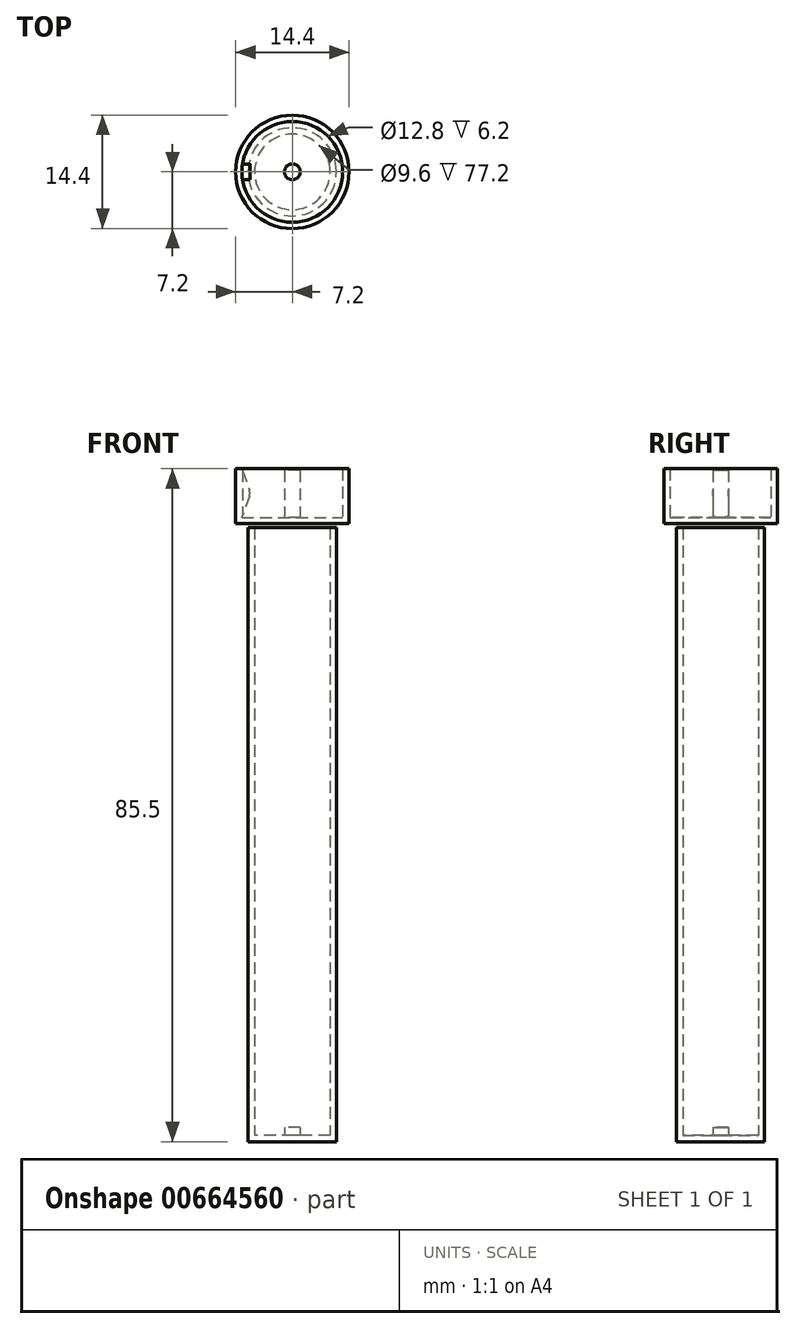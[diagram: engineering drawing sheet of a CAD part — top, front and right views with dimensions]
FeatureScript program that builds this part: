
annotation { "Feature Type Name" : "Feature", "Feature Type Description" : "" }
export const myFeature = defineFeature(function(context is Context, id is Id, definition is map)
    precondition{}
    {
        {
            var Q0;
            Q0=qCreatedBy(makeId("Top.planeOp"),FACE);
            var sketch = newSketch(context, id + "F0", { "sketchPlane" : qUnion([Q0])});
            skCircle(sketch, "E0", {"center": v(0, 0) * mm, "radius": 5.6 * mm});
            skSolve(sketch);
        }
        {
            var Q0;
            Q0=makeQuery(id+"F0.imprint","IMPRINT",FACE,{"disambiguationData":[TD([[makeQuery(id+"F0.imprint","IMPRINT",EDGE,{"derivedFrom":sQuery(id+"F0.wireOp",EDGE,"E0")}),1.0]])]});
            extrude(context, id + "F1", {"entities" : qUnion([Q0]), "depth" : 78 * mm, "offsetDistance" : 25 * mm});
        }
        {
            var Q0;
            Q0=makeQuery(id+"F1.opExtrude","CAP_FACE",FACE,{"disambiguationData":[OSD([sQuery(id+"F0.wireOp",EDGE,"E0")])],"isStart":false});
            shell(context, id + "F2", {"entities" : qUnion([Q0]), "thickness" : 0.8 * mm});
        }
        {
            var Q0;
            {var subQ0=sQuery(id+"F0.wireOp",EDGE,"E0");Q0=makeQuery(id+"F2.opShell","OFFSET_FACE",FACE,{"disambiguationData":[OSD([subQ0]),TDD([makeQuery(id+"F1.opExtrude","CAP_FACE",FACE,{"disambiguationData":[OSD([subQ0])],"isStart":true})])]});}
            var sketch = newSketch(context, id + "F3", { "sketchPlane" : qUnion([Q0])});
            skCircle(sketch, "E1", {"center": v(0, 0) * mm, "radius": 1 * mm});
            skSolve(sketch);
        }
        {
            var Q0;
            Q0 = qSketchRegion(id + "F3", true);
            extrude(context, id + "F4", {"entities" : qUnion([Q0]), "operationType" : NewBodyOperationType.ADD, "depth" : 1 * mm, "offsetDistance" : 25 * mm});
        }
        {
            var Q0;
            Q0=makeQuery(id+"F1.opExtrude","CAP_FACE",FACE,{"disambiguationData":[OSD([sQuery(id+"F0.wireOp",EDGE,"E0")])],"isStart":false});
            cPlane(context, id + "F5", {"entities" : qUnion([Q0]), "cplaneType" : CPlaneType.OFFSET, "offset" : 0.5 * mm, "width" : 150 * mm, "height" : 150 * mm});
        }
        {
            var Q0;
            Q0=qCreatedBy(id+"F5.planeOp",FACE);
            var sketch = newSketch(context, id + "F6", { "sketchPlane" : qUnion([Q0])});
            skCircle(sketch, "E2", {"center": v(0, 0) * mm, "radius": 7.2 * mm});
            skSolve(sketch);
        }
        {
            var Q0;
            Q0=makeQuery(id+"F6.imprint","IMPRINT",FACE,{"disambiguationData":[TD([[makeQuery(id+"F6.imprint","IMPRINT",EDGE,{"derivedFrom":sQuery(id+"F6.wireOp",EDGE,"E2")}),1.0]])]});
            extrude(context, id + "F7", {"entities" : qUnion([Q0]), "depth" : 7 * mm, "offsetDistance" : 25 * mm});
        }
        {
            var Q0;
            Q0=makeQuery(id+"F7.opExtrude","CAP_FACE",FACE,{"disambiguationData":[OSD([sQuery(id+"F6.wireOp",EDGE,"E2")])],"isStart":false});
            shell(context, id + "F8", {"entities" : qUnion([Q0]), "thickness" : 0.8 * mm});
        }
        {
            var Q0;
            Q0=qCreatedBy(makeId("Front.planeOp"),FACE);
            var sketch = newSketch(context, id + "F9", { "sketchPlane" : qUnion([Q0])});
            skLineSegment(sketch, "E3", {"start": v(-6.4, 79.3) * mm, "end": v(-6.4, 85.5) * mm});
            skLineSegment(sketch, "E4", {"start": v(-6.4, 85.5) * mm, "end": v(-5.47, 82.8) * mm});
            skLineSegment(sketch, "E5", {"start": v(-5.47, 82) * mm, "end": v(-6.4, 79.3) * mm});
            skLineSegment(sketch, "E6", {"start": v(-5.33, 82.4) * mm, "end": v(-12.5, 82.4) * mm, "construction": true});
            skPoint(sketch, "E7.visualSharp", {"position": v(-5.33, 82.4) * mm});
            skArc(sketch, "E7.filletArc", {"start": v(-5.47, 82) * mm, "mid": v(-5.4, 82.4) * mm, "end": v(-5.47, 82.8) * mm});
            skPoint(sketch, "E8", {"position": v(-5.4, 82.4) * mm});
            skLineSegment(sketch, "E9", {"start": v(-5.6, 1) * mm, "end": v(-5.6, 94) * mm});
            skSolve(sketch);
        }
        {
            var Q0;
            Q0 = qSketchRegion(id + "F9", true);
            extrude(context, id + "F10", {"entities" : qUnion([Q0]), "operationType" : NewBodyOperationType.ADD, "depth" : 1 * mm, "offsetDistance" : 25 * mm, "hasSecondDirection" : true, "secondDirectionOppositeDirection" : true, "secondDirectionDepth" : 1 * mm});
        }
        {
            var Q0;
            {var subQ0=sQuery(id+"F6.wireOp",EDGE,"E2");Q0=makeQuery(id+"F8.opShell","OFFSET_FACE",FACE,{"disambiguationData":[OSD([subQ0]),TDD([makeQuery(id+"F7.opExtrude","CAP_FACE",FACE,{"disambiguationData":[OSD([subQ0])],"isStart":true})])]});}
            var sketch = newSketch(context, id + "F11", { "sketchPlane" : qUnion([Q0])});
            skCircle(sketch, "E10", {"center": v(0, 0) * mm, "radius": 1 * mm});
            skSolve(sketch);
        }
        {
            var Q0;
            Q0=makeQuery(id+"F11.imprint","IMPRINT",FACE,{"disambiguationData":[TD([[makeQuery(id+"F11.imprint","IMPRINT",EDGE,{"derivedFrom":sQuery(id+"F11.wireOp",EDGE,"E10")}),1.0]])]});
            extrude(context, id + "F12", {"entities" : qUnion([Q0]), "operationType" : NewBodyOperationType.ADD, "depth" : 6 * mm, "offsetDistance" : 25 * mm});
        }
    });
